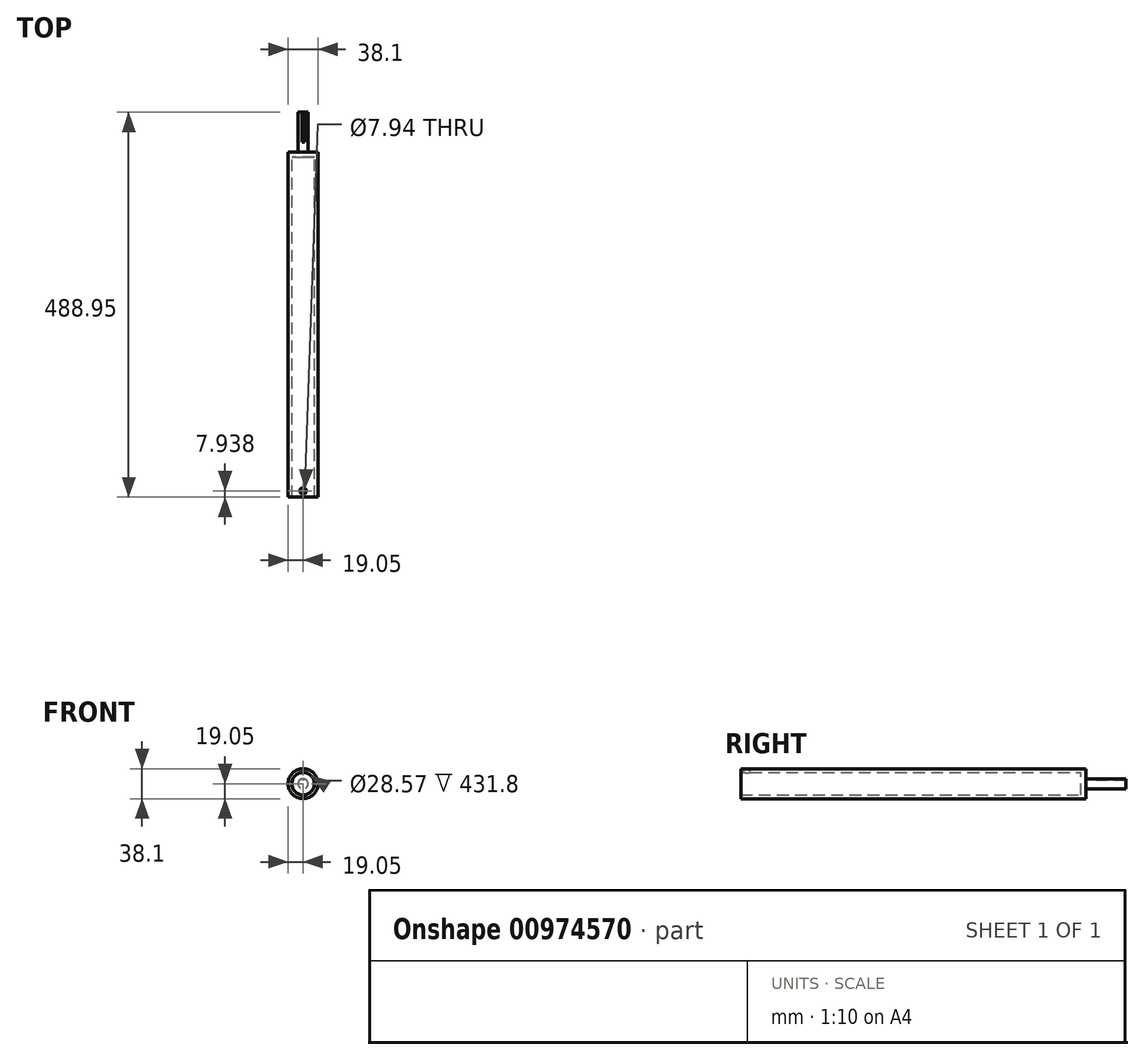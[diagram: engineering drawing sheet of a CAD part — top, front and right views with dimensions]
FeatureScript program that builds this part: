
annotation { "Feature Type Name" : "Feature", "Feature Type Description" : "" }
export const myFeature = defineFeature(function(context is Context, id is Id, definition is map)
    precondition{}
    {
        {
            var Q0;
            Q0=qCreatedBy(makeId("Front.planeOp"),FACE);
            var sketch = newSketch(context, id + "F0", { "sketchPlane" : qUnion([Q0])});
            skCircle(sketch, "E0", {"center": v(0, 0) * mm, "radius": 14.29 * mm});
            skCircle(sketch, "E1", {"center": v(0, 0) * mm, "radius": 19.05 * mm});
            skSolve(sketch);
        }
        {
            var Q0;
            Q0 = qSketchRegion(id + "F0", true);
            extrude(context, id + "F1", {"entities" : qUnion([Q0]), "depth" : 431.8 * mm, "offsetDistance" : 25.4 * mm});
        }
        {
            var Q0;
            Q0=makeQuery(id+"F1.opExtrude","CAP_FACE",FACE,{"disambiguationData":[OSD([sQuery(id+"F0.wireOp",EDGE,"E0"),sQuery(id+"F0.wireOp",EDGE,"E1")])],"isStart":true});
            var sketch = newSketch(context, id + "F2", { "sketchPlane" : qUnion([Q0])});
            skCircle(sketch, "E2", {"center": v(0, 0) * mm, "radius": 19.05 * mm});
            skSolve(sketch);
        }
        {
            var Q0;
            Q0 = qSketchRegion(id + "F2", true);
            extrude(context, id + "F3", {"entities" : qUnion([Q0]), "operationType" : NewBodyOperationType.ADD, "depth" : 6.35 * mm, "offsetDistance" : 25.4 * mm});
        }
        {
            var Q0;
            Q0=makeQuery(id+"F3.opExtrude","CAP_FACE",FACE,{"disambiguationData":[OSD([sQuery(id+"F2.wireOp",EDGE,"E2")])],"isStart":false});
            var sketch = newSketch(context, id + "F4", { "sketchPlane" : qUnion([Q0])});
            skCircle(sketch, "E3", {"center": v(0, 0) * mm, "radius": 6.35 * mm});
            skSolve(sketch);
        }
        {
            var Q0;
            Q0 = qSketchRegion(id + "F4", true);
            extrude(context, id + "F5", {"entities" : qUnion([Q0]), "operationType" : NewBodyOperationType.ADD, "depth" : 50.8 * mm, "offsetDistance" : 25.4 * mm});
        }
        {
            var Q0;
            Q0=makeQuery(id+"F5.opExtrude","CAP_FACE",FACE,{"disambiguationData":[OSD([sQuery(id+"F4.wireOp",EDGE,"E3")])],"isStart":false});
            var sketch = newSketch(context, id + "F6", { "sketchPlane" : qUnion([Q0])});
            skLineSegment(sketch, "E4", {"start": v(0, 0) * mm, "end": v(0, 6.35) * mm});
            skLineSegment(sketch, "E5", {"start": v(0, 6.35) * mm, "end": v(1.61, 6.35) * mm});
            skLineSegment(sketch, "E6", {"start": v(1.61, 6.35) * mm, "end": v(0, 6.35) * mm});
            skLineSegment(sketch, "E7", {"start": v(0, 6.35) * mm, "end": v(-1.61, 6.35) * mm});
            skLineSegment(sketch, "E8", {"start": v(-1.61, 6.35) * mm, "end": v(-1.61, 4.57) * mm});
            skLineSegment(sketch, "E9", {"start": v(-1.61, 4.57) * mm, "end": v(1.61, 4.57) * mm});
            skLineSegment(sketch, "E10", {"start": v(1.61, 4.57) * mm, "end": v(1.61, 6.35) * mm});
            skSolve(sketch);
        }
        {
            var Q0;
            Q0 = qSketchRegion(id + "F6", true);
            extrude(context, id + "F7", {"entities" : qUnion([Q0]), "operationType" : NewBodyOperationType.REMOVE, "oppositeDirection" : true, "depth" : 38.1 * mm, "offsetDistance" : 25.4 * mm});
        }
        {
            var Q0;
            Q0=qCreatedBy(makeId("Top.planeOp"),FACE);
            cPlane(context, id + "F8", {"entities" : qUnion([Q0]), "cplaneType" : CPlaneType.OFFSET, "offset" : 19.05 * mm, "width" : 152.4 * mm, "height" : 152.4 * mm});
        }
        {
            var Q0;
            Q0=qCreatedBy(id+"F8.planeOp",FACE);
            var sketch = newSketch(context, id + "F9", { "sketchPlane" : qUnion([Q0])});
            skLineSegment(sketch, "E11", {"start": v(0, 0) * mm, "end": v(0, -423.86) * mm});
            skCircle(sketch, "E12", {"center": v(0, -423.86) * mm, "radius": 3.97 * mm});
            skSolve(sketch);
        }
        {
            var Q0;
            Q0 = qSketchRegion(id + "F9", true);
            extrude(context, id + "F10", {"entities" : qUnion([Q0]), "operationType" : NewBodyOperationType.REMOVE, "oppositeDirection" : true, "depth" : 9.52 * mm, "offsetDistance" : 25.4 * mm});
        }
    });
